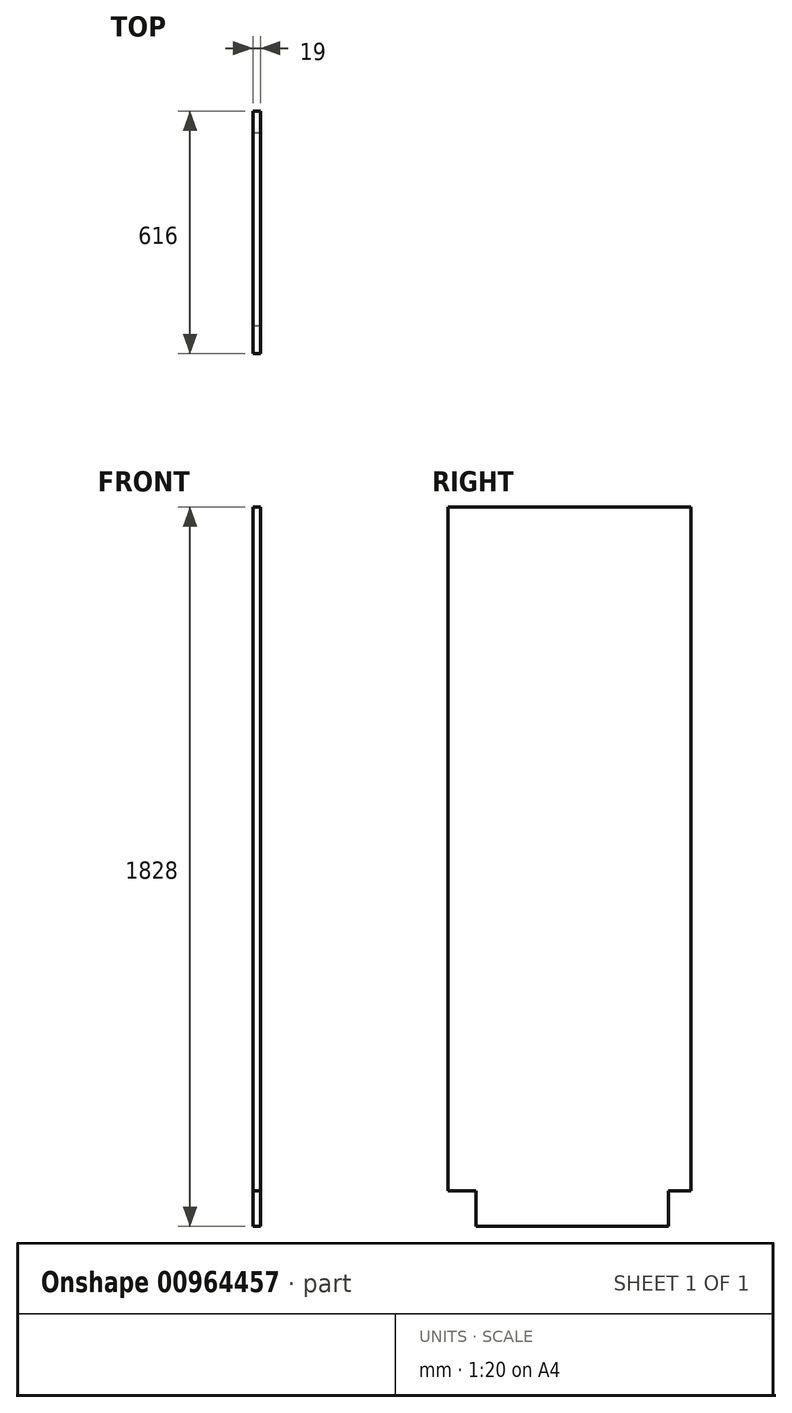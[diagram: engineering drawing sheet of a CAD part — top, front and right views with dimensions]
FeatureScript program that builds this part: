
annotation { "Feature Type Name" : "Feature", "Feature Type Description" : "" }
export const myFeature = defineFeature(function(context is Context, id is Id, definition is map)
    precondition{}
    {
        {
            var Q0;
            Q0=qCreatedBy(makeId("Right.planeOp"),FACE);
            var sketch = newSketch(context, id + "F0", { "sketchPlane" : qUnion([Q0])});
            skLineSegment(sketch, "E0.bottom", {"start": v(0, 0) * mm, "end": v(616, 0) * mm});
            skLineSegment(sketch, "E0.top", {"start": v(0, 1828) * mm, "end": v(616, 1828) * mm});
            skLineSegment(sketch, "E0.left", {"start": v(0, 0) * mm, "end": v(0, 1828) * mm});
            skLineSegment(sketch, "E0.right", {"start": v(616, 0) * mm, "end": v(616, 1828) * mm});
            skSolve(sketch);
        }
        {
            var Q0;
            Q0=makeQuery(id+"F0.imprint","IMPRINT",FACE,{"disambiguationData":[TD([[makeQuery(id+"F0.imprint","IMPRINT",EDGE,{"derivedFrom":sQuery(id+"F0.wireOp",EDGE,"E0.bottom")}),1.0]])]});
            extrude(context, id + "F1", {"entities" : qUnion([Q0]), "depth" : 19 * mm, "offsetDistance" : 25 * mm});
        }
        {
            var Q0;
            Q0=qCreatedBy(makeId("Right.planeOp"),FACE);
            var sketch = newSketch(context, id + "F2", { "sketchPlane" : qUnion([Q0])});
            skLineSegment(sketch, "E1.bottom", {"start": v(616, 0) * mm, "end": v(560, 0) * mm});
            skLineSegment(sketch, "E1.top", {"start": v(616, 90) * mm, "end": v(560, 90) * mm});
            skLineSegment(sketch, "E1.left", {"start": v(616, 0) * mm, "end": v(616, 90) * mm});
            skLineSegment(sketch, "E1.right", {"start": v(560, 0) * mm, "end": v(560, 90) * mm});
            skLineSegment(sketch, "E2.bottom", {"start": v(0, 0) * mm, "end": v(70, 0) * mm});
            skLineSegment(sketch, "E2.top", {"start": v(0, 90) * mm, "end": v(70, 90) * mm});
            skLineSegment(sketch, "E2.left", {"start": v(0, 0) * mm, "end": v(0, 90) * mm});
            skLineSegment(sketch, "E2.right", {"start": v(70, 0) * mm, "end": v(70, 90) * mm});
            skSolve(sketch);
        }
        {
            var Q0;
            Q0 = qSketchRegion(id + "F2", true);
            extrude(context, id + "F3", {"entities" : qUnion([Q0]), "operationType" : NewBodyOperationType.REMOVE, "endBound" : BoundingType.THROUGH_ALL, "depth" : 25 * mm, "offsetDistance" : 25 * mm});
        }
    });
